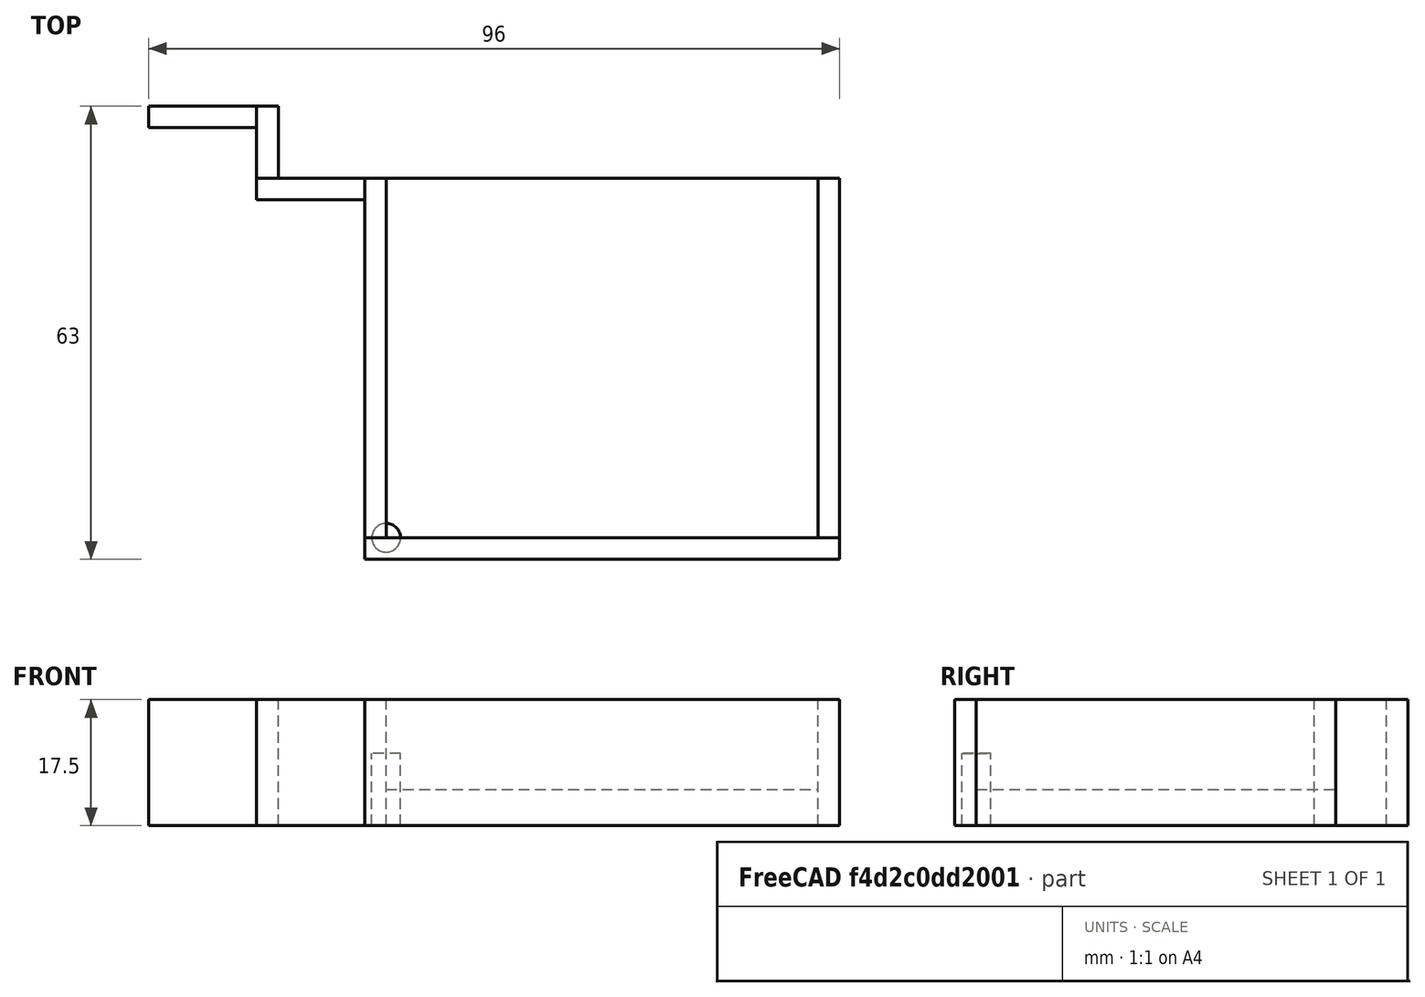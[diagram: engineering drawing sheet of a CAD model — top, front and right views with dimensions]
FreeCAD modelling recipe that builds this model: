
FCSTD DOCUMENT  (FreeCAD 0.15R4671 (Git))
Label: battery box
License: All rights reserved
LicenseURL: http://en.wikipedia.org/wiki/All_rights_reserved
objects: Part::Box×7, Part::Cylinder×1
note: 8 computed .brp shape members not serialized (recipe doc carries the construction recipe); baked Part::Feature solids carry a one-line shape summary decoded from their .brp

FEATURE [Part::Box] Box  label="base"
  Height = 5
  Length = 60
  Width = 50
FEATURE [Part::Box] Box001  label="side 001"
  Height = 17.5
  Length = 3
  Placement = pos=(60,0,0) rot=(0,0,1;0rad)
  Width = 50
FEATURE [Part::Box] Box002  label="side 002"
  Height = 17.5
  Length = 3
  Placement = pos=(-3,0,0) rot=(0,0,1;0rad)
  Width = 50
FEATURE [Part::Box] Box003  label="side 003"
  Height = 17.5
  Length = 15
  Placement = pos=(-18,47,0) rot=(0,0,1;0rad)
  Width = 3
FEATURE [Part::Box] Box004  label="side 004"
  Height = 17.5
  Length = 66
  Placement = pos=(-3,-3,0) rot=(0,0,1;0rad)
  Width = 3
FEATURE [Part::Box] Box005  label="side 005"
  Height = 17.5
  Length = 3
  Placement = pos=(-18,50,0) rot=(0,0,1;0rad)
  Width = 10
FEATURE [Part::Box] Box006  label="side 006"
  Height = 17.5
  Length = 15
  Placement = pos=(-33,57,0) rot=(0,0,1;0rad)
  Width = 3
FEATURE [Part::Cylinder] Cylinder
  Angle = 360
  Height = 10
  Radius = 2
